# Revit family: DOMO SENSIA U
name_source: partatom
category: Aparatos sanitarios
revit_build: Autodesk Revit 2015 (Build: 20140223_1515(x64)
units: mm (PartAtom-declared; Revit-internal decimal feet)

## types (1)
- 79500
    CAUDAL = 1 L/Min
    Comentarios de tipo = roceso automático de adaptación al medio
◦Llave de paso integrada
◦Pack de batería estanco IP65 compuesto por una batería de 6 V
◦Intercambiable con grifos PRESTO: 12, 12 A, 312, 312 A, 12 PS, 12 A PS, 312 PS, 312 A PS
◦Presión de uso recomendada: 1-5 bar (min, 0,8 – max 8 bar)
◦Peso bruto: 1,100 kg
◦Ahorro de agua y energía
◦Componentes integrados: mantenimiento sencillo y excelente estanqueidad
◦Conexiones internas estancas
◦Cierre automático en caso de pila agotada, indicación de batería baja mediante LED de comunicación
◦Aclarado automático cada 24h
◦Indicador de batería baja mediante LED de comunicación
◦Suministrado con: Batería CPR2
◦Embellecedor
◦Tubo de efecto agua de Ø 16 mm
    Conexión AC = Sí
    Conexión AF = Sí
    Código de montaje = C1030220
    Descripción = Grifo electrónico para urinario, fijación mural.
    ENTRADA = Macho 1/2"
    Elevación por defecto = 1219 mm
    Fabricante = PRESTO IBÉRICA
    Imagen de tipo = <Ninguno>
    Material = LATON NIQUELADO
    Modelo = PRESTO DOMO SENSIA U
    PESO BRUTO = 1.100 Kg
    Presión Máxima = 8 bar
    REFERENCIA = 79500
    Teléfono = (+34) 915 782 575
    URL = http://www.prestoiberica.com

## geometry (parser evidence)
native form markers: Blend x3
no freeform markers — native parametric forms only
